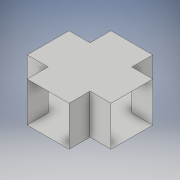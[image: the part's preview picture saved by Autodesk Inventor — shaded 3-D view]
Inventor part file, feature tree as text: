
AUTODESK INVENTOR PART (.ipt)
format: ipt  version: 2017 (Build 210142000, 142)  size: 109,568 bytes
history: native  units: in
note: dims shown in document units (in); Inventor stores cm internally (conversion verified against a paired STEP export)
features: extrude x1, pattern_circular x1, other x1, sketch x1
ambient origin geometry x8: Origin, YZ Plane, XZ Plane, XY Plane, X Axis, Y Axis, Z Axis, Center Point
bodies: Solid1 (feature_tree)
feature tree (4):
  extrude  "corridors"  Depth=6.6667in
  pattern_circular  "3 more corridors"  [2 undecoded]
  other  "enterences"
  sketch  "Sketch1"  dims[d0=7.0in d1=6.6667in d2=7.0in d3=0.0in d4=1.5748in d5=360.0deg]
note: 2 required parameter values undecoded (feature->parameter linkage not recoverable at this tier; creation-order binding heuristic only, values carry confidence <= 0.55)
